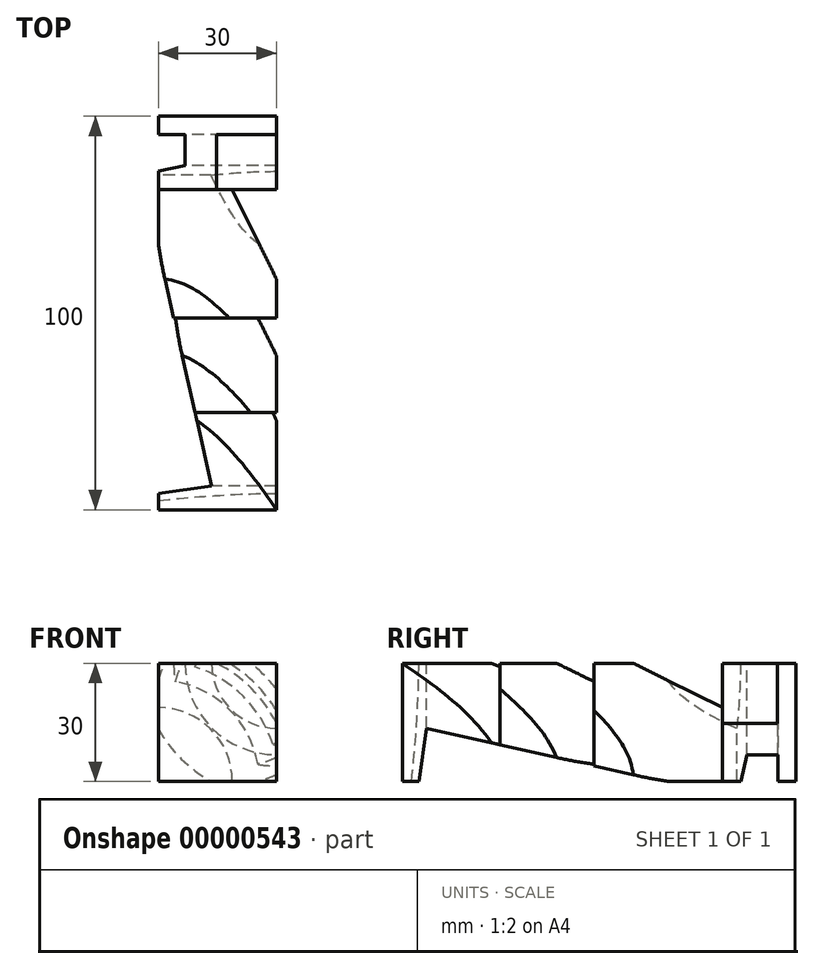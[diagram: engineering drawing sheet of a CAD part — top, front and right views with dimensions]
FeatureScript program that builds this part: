
annotation { "Feature Type Name" : "Feature", "Feature Type Description" : "" }
export const myFeature = defineFeature(function(context is Context, id is Id, definition is map)
    precondition{}
    {
        {
            var Q0;
            Q0=qCreatedBy(makeId("Front.planeOp"),FACE);
            var sketch = newSketch(context, id + "F0", { "sketchPlane" : qUnion([Q0])});
            skLineSegment(sketch, "E0.bottom", {"start": v(0, 0) * mm, "end": v(30, 0) * mm});
            skLineSegment(sketch, "E0.top", {"start": v(0, 30) * mm, "end": v(30, 30) * mm});
            skLineSegment(sketch, "E0.left", {"start": v(0, 0) * mm, "end": v(0, 30) * mm});
            skLineSegment(sketch, "E0.right", {"start": v(30, 0) * mm, "end": v(30, 30) * mm});
            skSolve(sketch);
        }
        {
            var Q0;
            Q0=makeQuery(id+"F0.imprint","IMPRINT",FACE,{"disambiguationData":[TD([[makeQuery(id+"F0.imprint","IMPRINT",EDGE,{"derivedFrom":sQuery(id+"F0.wireOp",EDGE,"E0.bottom")}),1.0]])]});
            extrude(context, id + "F1", {"entities" : qUnion([Q0]), "depth" : 100 * mm});
        }
        {
            var Q0;
            Q0=makeQuery(id+"F1.opExtrude","CAP_VERTEX",VERTEX,{"disambiguationData":[OSD([sQuery(id+"F0.wireOp",EDGE,"E0.bottom"),sQuery(id+"F0.wireOp",EDGE,"E0.left")])],"isStart":false});
            var Q1;
            Q1=makeQuery(id+"F1.opExtrude","CAP_VERTEX",VERTEX,{"disambiguationData":[OSD([sQuery(id+"F0.wireOp",EDGE,"E0.top"),sQuery(id+"F0.wireOp",EDGE,"E0.right")])],"isStart":false});
            var Q2;
            Q2=makeQuery(id+"F1.opExtrude","CAP_VERTEX",VERTEX,{"disambiguationData":[OSD([sQuery(id+"F0.wireOp",EDGE,"E0.top"),sQuery(id+"F0.wireOp",EDGE,"E0.right")])],"isStart":true});
            cPlane(context, id + "F2", {"entities" : qUnion([Q0, Q1, Q2]), "cplaneType" : CPlaneType.THREE_POINT, "offset" : 150 * mm, "width" : 150 * mm, "height" : 150 * mm});
        }
        {
            var Q0;
            Q0=qCreatedBy(id+"F2.planeOp",FACE);
            var sketch = newSketch(context, id + "F3", { "sketchPlane" : qUnion([Q0])});
            skLineSegment(sketch, "E1.0", {"start": v(-100, 0) * mm, "end": v(0, 0) * mm, "construction": true});
            skLineSegment(sketch, "E2.0", {"start": v(-100, 42.43) * mm, "end": v(0, 42.43) * mm});
            skLineSegment(sketch, "E3", {"start": v(-100, 42.43) * mm, "end": v(-75.26, 30.54) * mm});
            skLineSegment(sketch, "E4", {"start": v(-75.26, 30.54) * mm, "end": v(-75.26, 38.09) * mm});
            skLineSegment(sketch, "E5", {"start": v(-75.26, 38.09) * mm, "end": v(-51.3, 25.66) * mm});
            skLineSegment(sketch, "E6", {"start": v(-51.3, 25.66) * mm, "end": v(-51.3, 34.98) * mm});
            skLineSegment(sketch, "E7", {"start": v(-51.3, 34.98) * mm, "end": v(-18.66, 18.78) * mm});
            skLineSegment(sketch, "E8", {"start": v(-18.66, 18.78) * mm, "end": v(-18.66, 33.42) * mm});
            skLineSegment(sketch, "E9", {"start": v(-18.66, 33.42) * mm, "end": v(-4.68, 33.42) * mm});
            skLineSegment(sketch, "E10", {"start": v(-4.68, 33.42) * mm, "end": v(-4.68, 42.43) * mm});
            skSolve(sketch);
        }
        {
            var Q0;
            Q0=qCreatedBy(id+"F2.planeOp",FACE);
            var sketch = newSketch(context, id + "F4", { "sketchPlane" : qUnion([Q0])});
            skLineSegment(sketch, "E11.0", {"start": v(-100, 0) * mm, "end": v(0, 0) * mm});
            skLineSegment(sketch, "E12", {"start": v(-97.63, 0) * mm, "end": v(-93.9, 25.93) * mm});
            skLineSegment(sketch, "E13", {"start": v(-93.9, 25.93) * mm, "end": v(-14.96, 8.14) * mm});
            skLineSegment(sketch, "E14", {"start": v(-14.96, 8.14) * mm, "end": v(-12.5, 19.2) * mm});
            skLineSegment(sketch, "E15", {"start": v(-12.5, 19.2) * mm, "end": v(-4.62, 19.2) * mm});
            skLineSegment(sketch, "E16", {"start": v(-4.62, 19.2) * mm, "end": v(-4.62, 0) * mm});
            skLineSegment(sketch, "E17.0", {"start": v(-100, 42.43) * mm, "end": v(0, 42.43) * mm, "construction": true});
            skSolve(sketch);
        }
        {
            var Q0;
            {var subQ1=sQuery(id+"F3.wireOp",EDGE,"E3");Q0=makeQuery(id+"F3.imprint","IMPRINT",FACE,{"disambiguationData":[TD([[makeQuery(id+"F3.imprint","IMPRINT",EDGE,{"derivedFrom":subQ1}),1.0]])]});}
            var Q1;
            Q1=sQuery(id+"F3.wireOp",EDGE,"E1.0");
            revolve(context, id + "F5", {"operationType" : NewBodyOperationType.REMOVE, "entities" : qUnion([Q0]), "axis" : qUnion([Q1]), "revolveType" : RevolveType.FULL, "oppositeDirection" : true});
        }
        {
            var Q0;
            {var subQ1=sQuery(id+"F4.wireOp",EDGE,"E12");Q0=makeQuery(id+"F4.imprint","IMPRINT",FACE,{"disambiguationData":[TD([[makeQuery(id+"F4.imprint","IMPRINT",EDGE,{"derivedFrom":subQ1}),-1.0]])]});}
            var Q1;
            Q1=sQuery(id+"F4.wireOp",EDGE,"E17.0");
            revolve(context, id + "F6", {"operationType" : NewBodyOperationType.REMOVE, "entities" : qUnion([Q0]), "axis" : qUnion([Q1]), "revolveType" : RevolveType.FULL, "oppositeDirection" : true});
        }
    });
